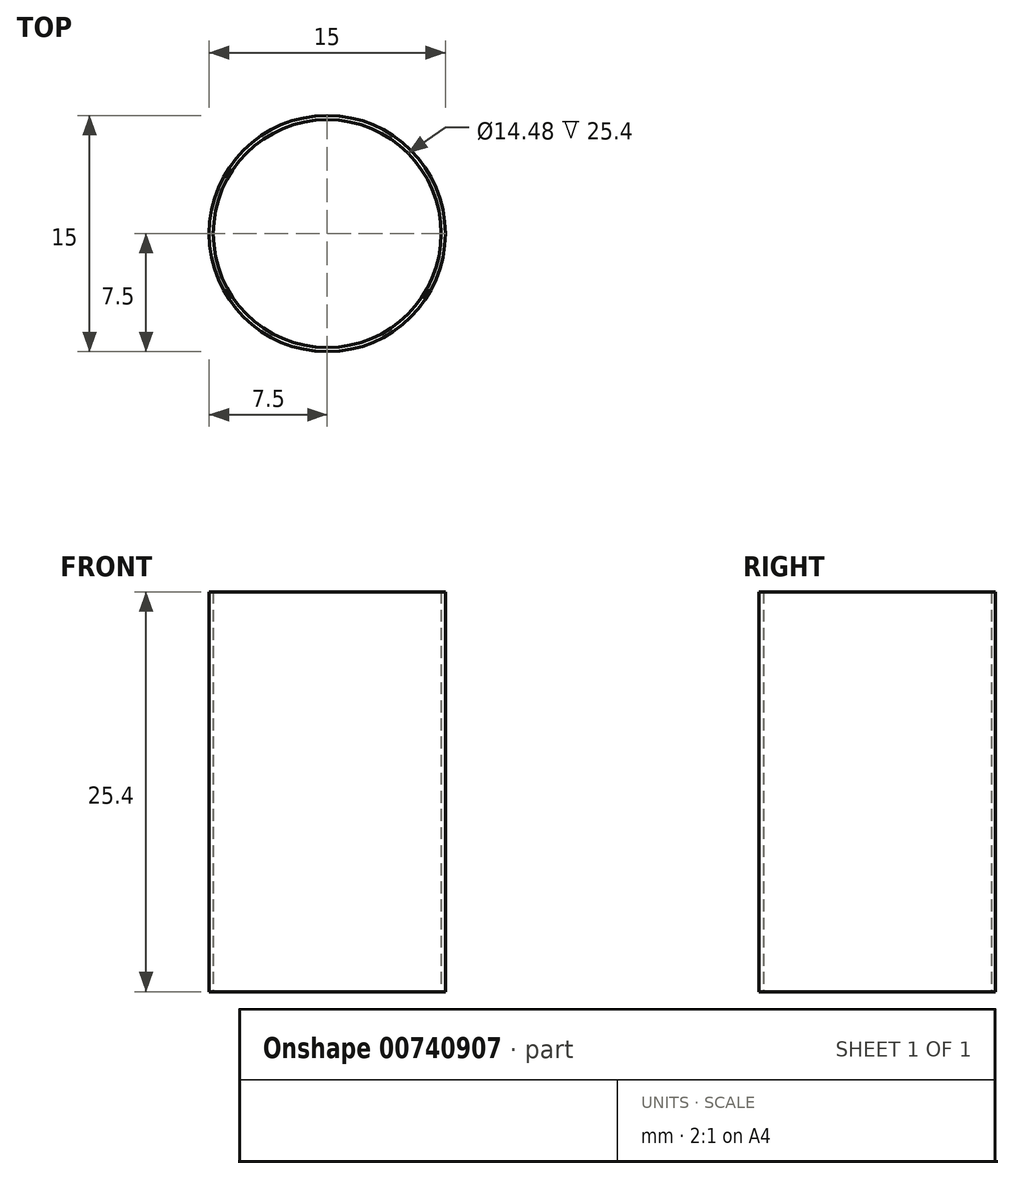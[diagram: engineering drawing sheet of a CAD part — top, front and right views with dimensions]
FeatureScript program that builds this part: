
annotation { "Feature Type Name" : "Feature", "Feature Type Description" : "" }
export const myFeature = defineFeature(function(context is Context, id is Id, definition is map)
    precondition{}
    {
        {
            var Q0;
            Q0=qCreatedBy(makeId("Top.planeOp"),FACE);
            var sketch = newSketch(context, id + "F0", { "sketchPlane" : qUnion([Q0])});
            skCircle(sketch, "E0", {"center": v(0, 0) * mm, "radius": 7.5 * mm});
            skCircle(sketch, "E1", {"center": v(0, 0) * mm, "radius": 7.24 * mm});
            skSolve(sketch);
        }
        {
            var Q0;
            Q0=makeQuery(id+"F0.imprint","IMPRINT",FACE,{"disambiguationData":[TD([[makeQuery(id+"F0.imprint","IMPRINT",EDGE,{"derivedFrom":sQuery(id+"F0.wireOp",EDGE,"E0")}),1.0]])]});
            extrude(context, id + "F1", {"entities" : qUnion([Q0]), "depth" : 25.4 * mm, "offsetDistance" : 25.4 * mm});
        }
    });
